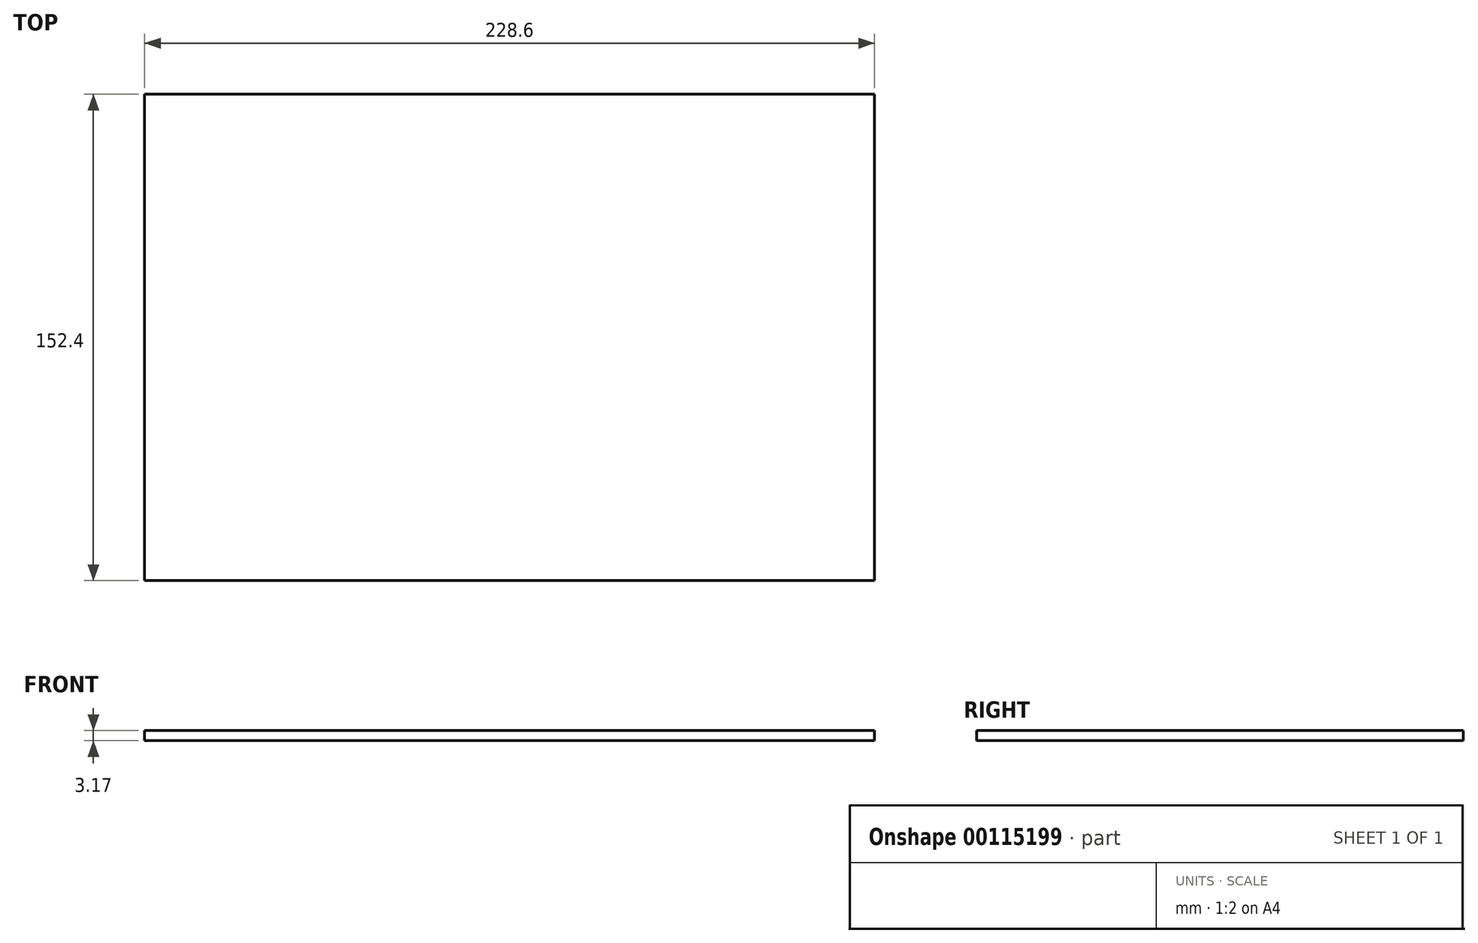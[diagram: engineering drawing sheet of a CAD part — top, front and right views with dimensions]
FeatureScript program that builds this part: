
annotation { "Feature Type Name" : "Feature", "Feature Type Description" : "" }
export const myFeature = defineFeature(function(context is Context, id is Id, definition is map)
    precondition{}
    {
        {
            var Q0;
            Q0=qCreatedBy(makeId("Top.planeOp"),FACE);
            var sketch = newSketch(context, id + "F0", { "sketchPlane" : qUnion([Q0])});
            skLineSegment(sketch, "E0.bottom", {"start": v(-114.3, -76.2) * mm, "end": v(114.3, -76.2) * mm});
            skLineSegment(sketch, "E0.top", {"start": v(-114.3, 76.2) * mm, "end": v(114.3, 76.2) * mm});
            skLineSegment(sketch, "E0.left", {"start": v(-114.3, -76.2) * mm, "end": v(-114.3, 76.2) * mm});
            skLineSegment(sketch, "E0.right", {"start": v(114.3, -76.2) * mm, "end": v(114.3, 76.2) * mm});
            skPoint(sketch, "E0.middle", {"position": v(0, 0) * mm});
            skSolve(sketch);
        }
        {
            var Q0;
            Q0=makeQuery(id+"F0.imprint","IMPRINT",FACE,{"disambiguationData":[TD([[makeQuery(id+"F0.imprint","IMPRINT",EDGE,{"derivedFrom":sQuery(id+"F0.wireOp",EDGE,"E0.bottom")}),1.0]])]});
            extrude(context, id + "F1", {"entities" : qUnion([Q0]), "depth" : 3.17 * mm});
        }
    });
